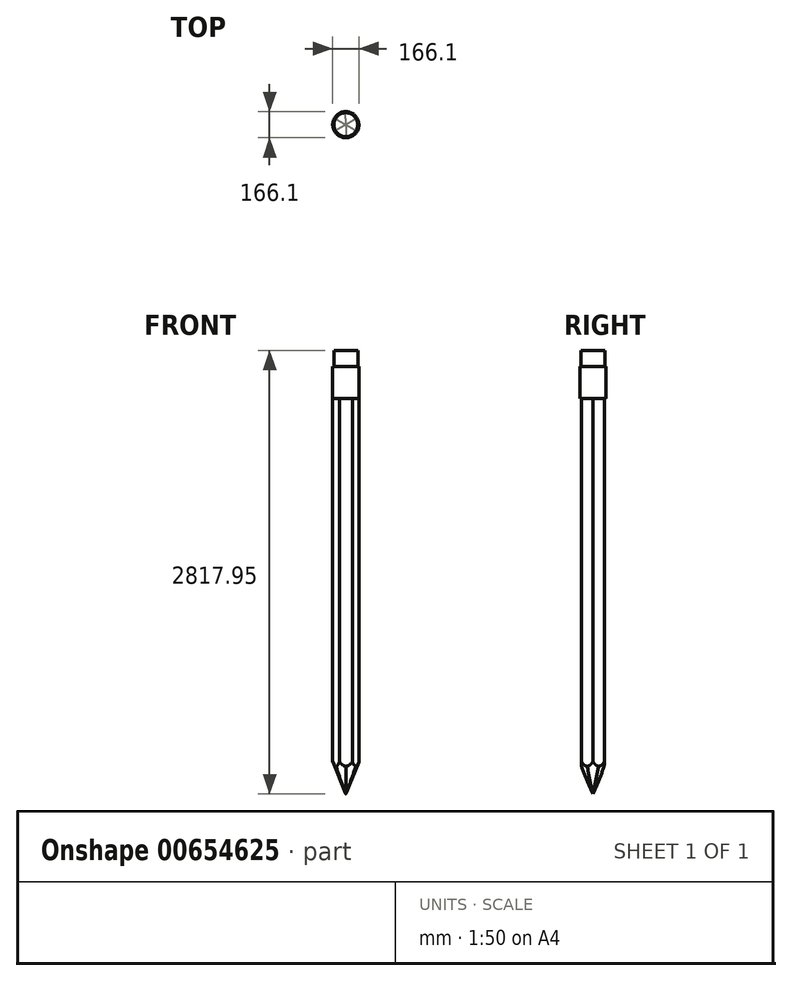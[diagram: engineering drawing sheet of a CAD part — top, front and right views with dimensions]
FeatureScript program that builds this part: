
annotation { "Feature Type Name" : "Feature", "Feature Type Description" : "" }
export const myFeature = defineFeature(function(context is Context, id is Id, definition is map)
    precondition{}
    {
        {
            var Q0;
            Q0=qCreatedBy(makeId("Top.planeOp"),FACE);
            var sketch = newSketch(context, id + "F0", { "sketchPlane" : qUnion([Q0])});
            skCircle(sketch, "E0.cCircle", {"center": v(0, 0) * mm, "radius": 71.93 * mm, "construction": true});
            skLineSegment(sketch, "E0.0", {"start": v(83.05, 0.74) * mm, "end": v(42.16, -71.56) * mm});
            skLineSegment(sketch, "E0.1", {"start": v(42.16, -71.56) * mm, "end": v(-40.89, -72.3) * mm});
            skLineSegment(sketch, "E0.2", {"start": v(-40.89, -72.3) * mm, "end": v(-83.05, -0.74) * mm});
            skLineSegment(sketch, "E0.3", {"start": v(-83.05, -0.74) * mm, "end": v(-42.16, 71.56) * mm});
            skLineSegment(sketch, "E0.4", {"start": v(-42.16, 71.56) * mm, "end": v(40.89, 72.3) * mm});
            skLineSegment(sketch, "E0.5", {"start": v(40.89, 72.3) * mm, "end": v(83.05, 0.74) * mm});
            skPoint(sketch, "E0.0.midPoint", {"position": v(62.6, -35.41) * mm});
            skSolve(sketch);
        }
        {
            var Q0;
            Q0=makeQuery(id+"F0.imprint","IMPRINT",FACE,{"disambiguationData":[TD([[makeQuery(id+"F0.imprint","IMPRINT",EDGE,{"derivedFrom":sQuery(id+"F0.wireOp",EDGE,"E0.0")}),-1.0]])]});
            extrude(context, id + "F1", {"entities" : qUnion([Q0]), "depth" : 2540 * mm, "offsetDistance" : 25.4 * mm});
        }
        {
            var Q0;
            Q0=makeQuery(id+"F1.opExtrude","CAP_FACE",FACE,{"disambiguationData":[OSD([sQuery(id+"F0.wireOp",EDGE,"E0.0"),sQuery(id+"F0.wireOp",EDGE,"E0.1"),sQuery(id+"F0.wireOp",EDGE,"E0.2"),sQuery(id+"F0.wireOp",EDGE,"E0.3"),sQuery(id+"F0.wireOp",EDGE,"E0.4"),sQuery(id+"F0.wireOp",EDGE,"E0.5")])],"isStart":false});
            var sketch = newSketch(context, id + "F2", { "sketchPlane" : qUnion([Q0])});
            skCircle(sketch, "E1", {"center": v(0, 0) * mm, "radius": 83.05 * mm});
            skSolve(sketch);
        }
        {
            var Q0;
            {var subQ1=makeQuery(id+"F1.opExtrude","CAP_EDGE",EDGE,{"disambiguationData":[OSD([sQuery(id+"F0.wireOp",EDGE,"E0.1")])],"isStart":false});Q0=makeQuery(id+"F2.imprint","IMPRINT",FACE,{"disambiguationData":[TD([[makeQuery(id+"F2.imprint","IMPRINT",EDGE,{"derivedFrom":subQ1}),1.0]])]});}
            var Q1;
            {var subQ1=makeQuery(id+"F1.opExtrude","CAP_EDGE",EDGE,{"disambiguationData":[OSD([sQuery(id+"F0.wireOp",EDGE,"E0.2")])],"isStart":false});Q1=makeQuery(id+"F2.imprint","IMPRINT",FACE,{"disambiguationData":[TD([[makeQuery(id+"F2.imprint","IMPRINT",EDGE,{"derivedFrom":subQ1}),1.0]])]});}
            var Q2;
            {var subQ1=makeQuery(id+"F1.opExtrude","CAP_EDGE",EDGE,{"disambiguationData":[OSD([sQuery(id+"F0.wireOp",EDGE,"E0.3")])],"isStart":false});Q2=makeQuery(id+"F2.imprint","IMPRINT",FACE,{"disambiguationData":[TD([[makeQuery(id+"F2.imprint","IMPRINT",EDGE,{"derivedFrom":subQ1}),1.0]])]});}
            var Q3;
            Q3=makeQuery(id+"F2.imprint","IMPRINT",FACE,{"disambiguationData":[TD([[makeQuery(id+"F2.imprint","IMPRINT",EDGE,{"derivedFrom":makeQuery(id+"F1.opExtrude","CAP_EDGE",EDGE,{"disambiguationData":[OSD([sQuery(id+"F0.wireOp",EDGE,"E0.0")])],"isStart":false})}),-1.0]])]});
            var Q4;
            {var subQ1=makeQuery(id+"F1.opExtrude","CAP_EDGE",EDGE,{"disambiguationData":[OSD([sQuery(id+"F0.wireOp",EDGE,"E0.0")])],"isStart":false});Q4=makeQuery(id+"F2.imprint","IMPRINT",FACE,{"disambiguationData":[TD([[makeQuery(id+"F2.imprint","IMPRINT",EDGE,{"derivedFrom":subQ1}),1.0]])]});}
            var Q5;
            {var subQ1=makeQuery(id+"F1.opExtrude","CAP_EDGE",EDGE,{"disambiguationData":[OSD([sQuery(id+"F0.wireOp",EDGE,"E0.5")])],"isStart":false});Q5=makeQuery(id+"F2.imprint","IMPRINT",FACE,{"disambiguationData":[TD([[makeQuery(id+"F2.imprint","IMPRINT",EDGE,{"derivedFrom":subQ1}),1.0]])]});}
            var Q6;
            {var subQ1=makeQuery(id+"F1.opExtrude","CAP_EDGE",EDGE,{"disambiguationData":[OSD([sQuery(id+"F0.wireOp",EDGE,"E0.4")])],"isStart":false});Q6=makeQuery(id+"F2.imprint","IMPRINT",FACE,{"disambiguationData":[TD([[makeQuery(id+"F2.imprint","IMPRINT",EDGE,{"derivedFrom":subQ1}),1.0]])]});}
            extrude(context, id + "F3", {"entities" : qUnion([Q0, Q1, Q2, Q3, Q4, Q5, Q6]), "operationType" : NewBodyOperationType.ADD, "depth" : 203.2 * mm, "offsetDistance" : 25.4 * mm});
        }
        {
            var Q0;
            Q0=makeQuery(id+"F3.opExtrude","CAP_FACE",FACE,{"disambiguationData":[OSD([sQuery(id+"F2.wireOp",EDGE,"E1")])],"isStart":false});
            var sketch = newSketch(context, id + "F4", { "sketchPlane" : qUnion([Q0])});
            skCircle(sketch, "E2", {"center": v(0, 0) * mm, "radius": 76.2 * mm});
            skSolve(sketch);
        }
        {
            var Q0;
            Q0=makeQuery(id+"F4.imprint","IMPRINT",FACE,{"disambiguationData":[TD([[makeQuery(id+"F4.imprint","IMPRINT",EDGE,{"derivedFrom":sQuery(id+"F4.wireOp",EDGE,"E2")}),1.0]])]});
            extrude(context, id + "F5", {"entities" : qUnion([Q0]), "operationType" : NewBodyOperationType.ADD, "depth" : 101.6 * mm, "offsetDistance" : 25.4 * mm});
        }
        {
            var Q0;
            Q0=makeQuery(id+"F1.opExtrude","CAP_FACE",FACE,{"disambiguationData":[OSD([sQuery(id+"F0.wireOp",EDGE,"E0.0"),sQuery(id+"F0.wireOp",EDGE,"E0.1"),sQuery(id+"F0.wireOp",EDGE,"E0.2"),sQuery(id+"F0.wireOp",EDGE,"E0.3"),sQuery(id+"F0.wireOp",EDGE,"E0.4"),sQuery(id+"F0.wireOp",EDGE,"E0.5")])],"isStart":true});
            chamfer(context, id + "F6", {"entities" : qUnion([Q0]), "chamferType" : ChamferType.TWO_OFFSETS, "width1" : 71.88 * mm, "oppositeDirection" : false, "width2" : 203.2 * mm, "tangentPropagation" : true});
        }
        {
            var Q0;
            Q0=makeQuery(id+"F6.opChamfer","BLEND_EDGE",EDGE,{"blendedFrom":[makeQuery(id+"F1.opExtrude","CAP_EDGE",EDGE,{"disambiguationData":[OSD([sQuery(id+"F0.wireOp",EDGE,"E0.4")])],"isStart":true}),makeQuery(id+"F1.opExtrude","CAP_EDGE",EDGE,{"disambiguationData":[OSD([sQuery(id+"F0.wireOp",EDGE,"E0.5")])],"isStart":true})],"blendedInto":[]});
            var Q1;
            Q1=makeQuery(id+"F6.opChamfer","BLEND_EDGE",EDGE,{"blendedFrom":[makeQuery(id+"F1.opExtrude","CAP_EDGE",EDGE,{"disambiguationData":[OSD([sQuery(id+"F0.wireOp",EDGE,"E0.3")])],"isStart":true}),makeQuery(id+"F1.opExtrude","CAP_EDGE",EDGE,{"disambiguationData":[OSD([sQuery(id+"F0.wireOp",EDGE,"E0.4")])],"isStart":true})],"blendedInto":[]});
            var Q2;
            Q2=makeQuery(id+"F6.opChamfer","BLEND_EDGE",EDGE,{"blendedFrom":[makeQuery(id+"F1.opExtrude","CAP_EDGE",EDGE,{"disambiguationData":[OSD([sQuery(id+"F0.wireOp",EDGE,"E0.2")])],"isStart":true}),makeQuery(id+"F1.opExtrude","CAP_EDGE",EDGE,{"disambiguationData":[OSD([sQuery(id+"F0.wireOp",EDGE,"E0.3")])],"isStart":true})],"blendedInto":[]});
            var Q3;
            Q3=makeQuery(id+"F6.opChamfer","BLEND_EDGE",EDGE,{"blendedFrom":[makeQuery(id+"F1.opExtrude","CAP_EDGE",EDGE,{"disambiguationData":[OSD([sQuery(id+"F0.wireOp",EDGE,"E0.1")])],"isStart":true}),makeQuery(id+"F1.opExtrude","CAP_EDGE",EDGE,{"disambiguationData":[OSD([sQuery(id+"F0.wireOp",EDGE,"E0.2")])],"isStart":true})],"blendedInto":[]});
            var Q4;
            Q4=makeQuery(id+"F6.opChamfer","BLEND_EDGE",EDGE,{"blendedFrom":[makeQuery(id+"F1.opExtrude","CAP_EDGE",EDGE,{"disambiguationData":[OSD([sQuery(id+"F0.wireOp",EDGE,"E0.0")])],"isStart":true}),makeQuery(id+"F1.opExtrude","CAP_EDGE",EDGE,{"disambiguationData":[OSD([sQuery(id+"F0.wireOp",EDGE,"E0.1")])],"isStart":true})],"blendedInto":[]});
            var Q5;
            Q5=makeQuery(id+"F6.opChamfer","BLEND_EDGE",EDGE,{"blendedFrom":[makeQuery(id+"F1.opExtrude","CAP_EDGE",EDGE,{"disambiguationData":[OSD([sQuery(id+"F0.wireOp",EDGE,"E0.0")])],"isStart":true}),makeQuery(id+"F1.opExtrude","CAP_EDGE",EDGE,{"disambiguationData":[OSD([sQuery(id+"F0.wireOp",EDGE,"E0.5")])],"isStart":true})],"blendedInto":[]});
            fillet(context, id + "F7", {"entities" : qUnion([Q0, Q1, Q2, Q3, Q4, Q5]), "radius" : 76.2 * mm, "tangentPropagation" : true, "allowEdgeOverflow" : false});
        }
    });
